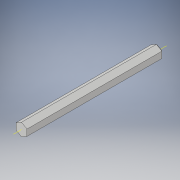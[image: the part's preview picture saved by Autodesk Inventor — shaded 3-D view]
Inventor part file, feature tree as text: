
AUTODESK INVENTOR PART (.ipt)
format: ipt  version: 2019 (Build 230136000, 136)  size: 121,856 bytes
history: native  units: in
note: dims shown in document units (in); Inventor stores cm internally (conversion verified against a paired STEP export)
features: sketch x2, extrude x1, other x1
ambient origin geometry x8: Origin, YZ Plane, XZ Plane, XY Plane, X Axis, Y Axis, Z Axis, Center Point
bodies: Solid2 (feature_tree), Solid1 (feature_tree)
feature tree (4):
  extrude  "Extrusion1"  [1 undecoded]
  sketch  "Sketch2"
  other  "Work Axis1"
  sketch  "Sketch1"  dims[d0=2.875in d1=0.0in]
note: 1 required parameter value undecoded (feature->parameter linkage not recoverable at this tier; creation-order binding heuristic only, values carry confidence <= 0.55)
